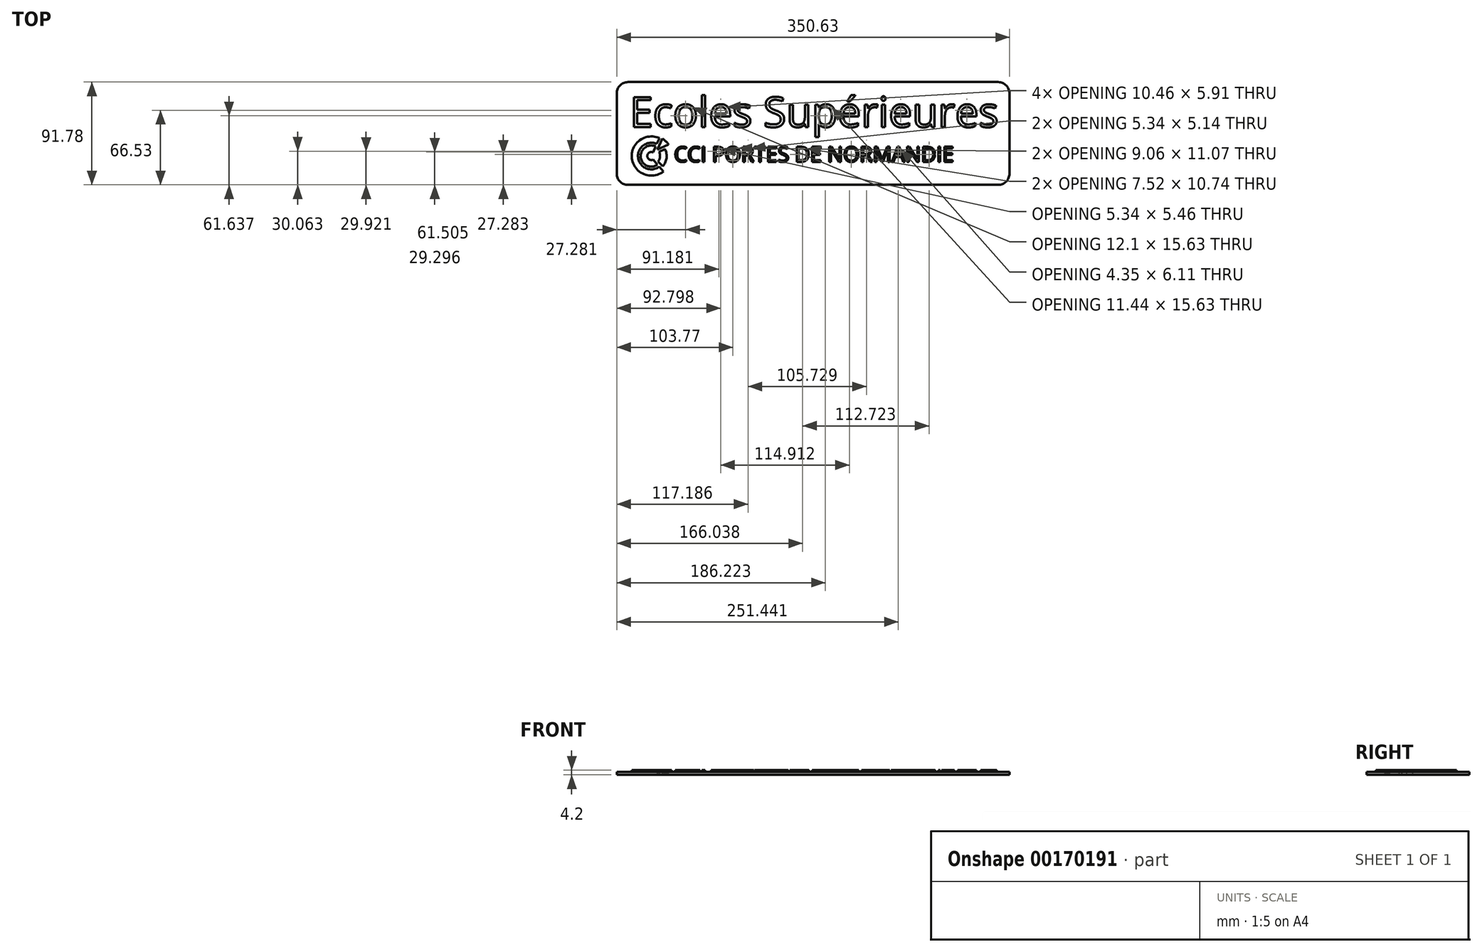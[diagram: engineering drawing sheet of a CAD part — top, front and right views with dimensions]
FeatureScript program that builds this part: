
annotation { "Feature Type Name" : "Feature", "Feature Type Description" : "" }
export const myFeature = defineFeature(function(context is Context, id is Id, definition is map)
    precondition{}
    {
        {
            var Q0;
            Q0=qCreatedBy(makeId("Top.planeOp"),FACE);
            var sketch = newSketch(context, id + "F0", { "sketchPlane" : qUnion([Q0])});
            skLineSegment(sketch, "E0.bottom", {"start": v(-153.76, 79.26) * mm, "end": v(196.24, 79.26) * mm});
            skLineSegment(sketch, "E0.top", {"start": v(-153.76, -13.12) * mm, "end": v(196.24, -13.12) * mm});
            skLineSegment(sketch, "E0.left", {"start": v(-153.76, 79.26) * mm, "end": v(-153.76, -13.12) * mm});
            skLineSegment(sketch, "E0.right", {"start": v(196.24, 79.26) * mm, "end": v(196.24, -13.12) * mm});
            skCircle(sketch, "E1", {"center": v(-123.39, 12.33) * mm, "radius": 17.49 * mm});
            skCircle(sketch, "E2", {"center": v(-123.39, 12.33) * mm, "radius": 11.88 * mm});
            skCircle(sketch, "E3", {"center": v(-123.39, 12.33) * mm, "radius": 9.49 * mm});
            skCircle(sketch, "E4", {"center": v(-123.39, 12.33) * mm, "radius": 3.6 * mm});
            skCircle(sketch, "E5", {"center": v(-123.39, 12.33) * mm, "radius": 7.83 * mm});
            skCircle(sketch, "E6", {"center": v(-123.39, 12.33) * mm, "radius": 13.72 * mm});
            skLineSegment(sketch, "E7", {"start": v(-123.39, 12.33) * mm, "end": v(-116.12, 28.24) * mm});
            skLineSegment(sketch, "E8", {"start": v(-112.54, -1.39) * mm, "end": v(-121.72, 9.15) * mm});
            skCircle(sketch, "E9", {"center": v(-123.39, 12.33) * mm, "radius": 18.48 * mm});
            skLineSegment(sketch, "E10", {"start": v(-118.04, 18.06) * mm, "end": v(-113.59, 28) * mm});
            skLineSegment(sketch, "E11", {"start": v(-118.04, 18.06) * mm, "end": v(-107.93, 22.47) * mm});
            skLineSegment(sketch, "E12", {"start": v(-116.5, 16.06) * mm, "end": v(-111.14, 18.51) * mm});
            skLineSegment(sketch, "E13", {"start": v(-117.25, 7.47) * mm, "end": v(-113.21, 3.13) * mm});
            skText(sketch, "E14", { "text": "Ecoles Supérieures", "fontName": "OpenSans-Regular.ttf"});
            skText(sketch, "E15", { "text": "CCI PORTES DE NORMANDIE", "fontName": "OpenSans-Regular.ttf"});
            const initialGuessF0  = {"E14": [-0.14265, 0.03824, 1, 0, 0.02692], "E15": [-0.10308, 0.00715, 1, 0, 0.01356]};
            skSetInitialGuess(sketch, initialGuessF0);
            skSolve(sketch);
        }
        {
            var Q0;
            Q0=makeQuery(id+"F0.imprint","IMPRINT",FACE,{"disambiguationData":[TD([[makeQuery(id+"F0.imprint","IMPRINT",EDGE,{"derivedFrom":sQuery(id+"F0.wireOp",EDGE,"E14.sketch_text.stroke-0")}),-1.0]])]});
            var Q1;
            Q1=makeQuery(id+"F0.imprint","IMPRINT",FACE,{"disambiguationData":[TD([[makeQuery(id+"F0.imprint","IMPRINT",EDGE,{"derivedFrom":sQuery(id+"F0.wireOp",EDGE,"E14.sketch_text.stroke-12")}),-1.0]])]});
            var Q2;
            Q2=makeQuery(id+"F0.imprint","IMPRINT",FACE,{"disambiguationData":[TD([[makeQuery(id+"F0.imprint","IMPRINT",EDGE,{"derivedFrom":sQuery(id+"F0.wireOp",EDGE,"E14.sketch_text.stroke-27")}),-1.0]])]});
            var Q3;
            Q3=makeQuery(id+"F0.imprint","IMPRINT",FACE,{"disambiguationData":[TD([[makeQuery(id+"F0.imprint","IMPRINT",EDGE,{"derivedFrom":sQuery(id+"F0.wireOp",EDGE,"E14.sketch_text.stroke-44")}),-1.0]])]});
            var Q4;
            Q4=makeQuery(id+"F0.imprint","IMPRINT",FACE,{"disambiguationData":[TD([[makeQuery(id+"F0.imprint","IMPRINT",EDGE,{"derivedFrom":sQuery(id+"F0.wireOp",EDGE,"E14.sketch_text.stroke-48")}),-1.0]])]});
            var Q5;
            Q5=makeQuery(id+"F0.imprint","IMPRINT",FACE,{"disambiguationData":[TD([[makeQuery(id+"F0.imprint","IMPRINT",EDGE,{"derivedFrom":sQuery(id+"F0.wireOp",EDGE,"E14.sketch_text.stroke-67")}),-1.0]])]});
            var Q6;
            Q6=makeQuery(id+"F0.imprint","IMPRINT",FACE,{"disambiguationData":[TD([[makeQuery(id+"F0.imprint","IMPRINT",EDGE,{"derivedFrom":sQuery(id+"F0.wireOp",EDGE,"E14.sketch_text.stroke-92")}),-1.0]])]});
            var Q7;
            Q7=makeQuery(id+"F0.imprint","IMPRINT",FACE,{"disambiguationData":[TD([[makeQuery(id+"F0.imprint","IMPRINT",EDGE,{"derivedFrom":sQuery(id+"F0.wireOp",EDGE,"E14.sketch_text.stroke-117")}),-1.0]])]});
            var Q8;
            Q8=makeQuery(id+"F0.imprint","IMPRINT",FACE,{"disambiguationData":[TD([[makeQuery(id+"F0.imprint","IMPRINT",EDGE,{"derivedFrom":sQuery(id+"F0.wireOp",EDGE,"E14.sketch_text.stroke-134")}),-1.0]])]});
            var Q9;
            Q9=makeQuery(id+"F0.imprint","IMPRINT",FACE,{"disambiguationData":[TD([[makeQuery(id+"F0.imprint","IMPRINT",EDGE,{"derivedFrom":sQuery(id+"F0.wireOp",EDGE,"E15.sketch_text.stroke-34")}),-1.0]])]});
            var Q10;
            Q10=makeQuery(id+"F0.imprint","IMPRINT",FACE,{"disambiguationData":[TD([[makeQuery(id+"F0.imprint","IMPRINT",EDGE,{"derivedFrom":sQuery(id+"F0.wireOp",EDGE,"E15.sketch_text.stroke-49")}),-1.0]])]});
            var Q11;
            Q11=makeQuery(id+"F0.imprint","IMPRINT",FACE,{"disambiguationData":[TD([[makeQuery(id+"F0.imprint","IMPRINT",EDGE,{"derivedFrom":sQuery(id+"F0.wireOp",EDGE,"E15.sketch_text.stroke-65")}),-1.0]])]});
            var Q12;
            Q12=makeQuery(id+"F0.imprint","IMPRINT",FACE,{"disambiguationData":[TD([[makeQuery(id+"F0.imprint","IMPRINT",EDGE,{"derivedFrom":sQuery(id+"F0.wireOp",EDGE,"E15.sketch_text.stroke-83")}),-1.0]])]});
            var Q13;
            Q13=makeQuery(id+"F0.imprint","IMPRINT",FACE,{"disambiguationData":[TD([[makeQuery(id+"F0.imprint","IMPRINT",EDGE,{"derivedFrom":sQuery(id+"F0.wireOp",EDGE,"E15.sketch_text.stroke-91")}),-1.0]])]});
            var Q14;
            Q14=makeQuery(id+"F0.imprint","IMPRINT",FACE,{"disambiguationData":[TD([[makeQuery(id+"F0.imprint","IMPRINT",EDGE,{"derivedFrom":sQuery(id+"F0.wireOp",EDGE,"E15.sketch_text.stroke-0")}),-1.0]])]});
            var Q15;
            Q15=makeQuery(id+"F0.imprint","IMPRINT",FACE,{"disambiguationData":[TD([[makeQuery(id+"F0.imprint","IMPRINT",EDGE,{"derivedFrom":sQuery(id+"F0.wireOp",EDGE,"E15.sketch_text.stroke-15")}),-1.0]])]});
            var Q16;
            Q16=makeQuery(id+"F0.imprint","IMPRINT",FACE,{"disambiguationData":[TD([[makeQuery(id+"F0.imprint","IMPRINT",EDGE,{"derivedFrom":sQuery(id+"F0.wireOp",EDGE,"E15.sketch_text.stroke-30")}),-1.0]])]});
            var Q17;
            Q17=makeQuery(id+"F0.imprint","IMPRINT",FACE,{"disambiguationData":[TD([[makeQuery(id+"F0.imprint","IMPRINT",EDGE,{"derivedFrom":sQuery(id+"F0.wireOp",EDGE,"E14.sketch_text.stroke-159")}),-1.0]])]});
            var Q18;
            Q18=makeQuery(id+"F0.imprint","IMPRINT",FACE,{"disambiguationData":[TD([[makeQuery(id+"F0.imprint","IMPRINT",EDGE,{"derivedFrom":sQuery(id+"F0.wireOp",EDGE,"E14.sketch_text.stroke-178")}),-1.0]])]});
            var Q19;
            Q19=makeQuery(id+"F0.imprint","IMPRINT",FACE,{"disambiguationData":[TD([[makeQuery(id+"F0.imprint","IMPRINT",EDGE,{"derivedFrom":sQuery(id+"F0.wireOp",EDGE,"E14.sketch_text.stroke-186")}),-1.0]])]});
            var Q20;
            Q20=makeQuery(id+"F0.imprint","IMPRINT",FACE,{"disambiguationData":[TD([[makeQuery(id+"F0.imprint","IMPRINT",EDGE,{"derivedFrom":sQuery(id+"F0.wireOp",EDGE,"E14.sketch_text.stroke-230")}),-1.0]])]});
            var Q21;
            Q21=makeQuery(id+"F0.imprint","IMPRINT",FACE,{"disambiguationData":[TD([[makeQuery(id+"F0.imprint","IMPRINT",EDGE,{"derivedFrom":sQuery(id+"F0.wireOp",EDGE,"E14.sketch_text.stroke-247")}),-1.0]])]});
            var Q22;
            Q22=makeQuery(id+"F0.imprint","IMPRINT",FACE,{"disambiguationData":[TD([[makeQuery(id+"F0.imprint","IMPRINT",EDGE,{"derivedFrom":sQuery(id+"F0.wireOp",EDGE,"E14.sketch_text.stroke-279")}),-1.0]])]});
            var Q23;
            Q23=makeQuery(id+"F0.imprint","IMPRINT",FACE,{"disambiguationData":[TD([[makeQuery(id+"F0.imprint","IMPRINT",EDGE,{"derivedFrom":sQuery(id+"F0.wireOp",EDGE,"E14.sketch_text.stroke-260")}),-1.0]])]});
            var Q24;
            Q24=makeQuery(id+"F0.imprint","IMPRINT",FACE,{"disambiguationData":[TD([[makeQuery(id+"F0.imprint","IMPRINT",EDGE,{"derivedFrom":sQuery(id+"F0.wireOp",EDGE,"E14.sketch_text.stroke-211")}),-1.0]])]});
            var Q25;
            Q25=makeQuery(id+"F0.imprint","IMPRINT",FACE,{"disambiguationData":[TD([[makeQuery(id+"F0.imprint","IMPRINT",EDGE,{"derivedFrom":sQuery(id+"F0.wireOp",EDGE,"E14.sketch_text.stroke-199")}),-1.0]])]});
            var Q26;
            Q26=makeQuery(id+"F0.imprint","IMPRINT",FACE,{"disambiguationData":[TD([[makeQuery(id+"F0.imprint","IMPRINT",EDGE,{"derivedFrom":sQuery(id+"F0.wireOp",EDGE,"E14.sketch_text.stroke-203")}),-1.0]])]});
            var Q27;
            Q27=makeQuery(id+"F0.imprint","IMPRINT",FACE,{"disambiguationData":[TD([[makeQuery(id+"F0.imprint","IMPRINT",EDGE,{"derivedFrom":sQuery(id+"F0.wireOp",EDGE,"E15.sketch_text.stroke-263")}),-1.0]])]});
            var Q28;
            Q28=makeQuery(id+"F0.imprint","IMPRINT",FACE,{"disambiguationData":[TD([[makeQuery(id+"F0.imprint","IMPRINT",EDGE,{"derivedFrom":sQuery(id+"F0.wireOp",EDGE,"E15.sketch_text.stroke-267")}),-1.0]])]});
            var Q29;
            Q29=makeQuery(id+"F0.imprint","IMPRINT",FACE,{"disambiguationData":[TD([[makeQuery(id+"F0.imprint","IMPRINT",EDGE,{"derivedFrom":sQuery(id+"F0.wireOp",EDGE,"E15.sketch_text.stroke-249")}),-1.0]])]});
            var Q30;
            Q30=makeQuery(id+"F0.imprint","IMPRINT",FACE,{"disambiguationData":[TD([[makeQuery(id+"F0.imprint","IMPRINT",EDGE,{"derivedFrom":sQuery(id+"F0.wireOp",EDGE,"E15.sketch_text.stroke-103")}),-1.0]])]});
            var Q31;
            Q31=makeQuery(id+"F0.imprint","IMPRINT",FACE,{"disambiguationData":[TD([[makeQuery(id+"F0.imprint","IMPRINT",EDGE,{"derivedFrom":sQuery(id+"F0.wireOp",EDGE,"E15.sketch_text.stroke-128")}),-1.0]])]});
            var Q32;
            Q32=makeQuery(id+"F0.imprint","IMPRINT",FACE,{"disambiguationData":[TD([[makeQuery(id+"F0.imprint","IMPRINT",EDGE,{"derivedFrom":sQuery(id+"F0.wireOp",EDGE,"E15.sketch_text.stroke-154")}),-1.0]])]});
            var Q33;
            Q33=makeQuery(id+"F0.imprint","IMPRINT",FACE,{"disambiguationData":[TD([[makeQuery(id+"F0.imprint","IMPRINT",EDGE,{"derivedFrom":sQuery(id+"F0.wireOp",EDGE,"E15.sketch_text.stroke-142")}),-1.0]])]});
            var Q34;
            Q34=makeQuery(id+"F0.imprint","IMPRINT",FACE,{"disambiguationData":[TD([[makeQuery(id+"F0.imprint","IMPRINT",EDGE,{"derivedFrom":sQuery(id+"F0.wireOp",EDGE,"E15.sketch_text.stroke-169")}),-1.0]])]});
            var Q35;
            Q35=makeQuery(id+"F0.imprint","IMPRINT",FACE,{"disambiguationData":[TD([[makeQuery(id+"F0.imprint","IMPRINT",EDGE,{"derivedFrom":sQuery(id+"F0.wireOp",EDGE,"E15.sketch_text.stroke-185")}),-1.0]])]});
            var Q36;
            Q36=makeQuery(id+"F0.imprint","IMPRINT",FACE,{"disambiguationData":[TD([[makeQuery(id+"F0.imprint","IMPRINT",EDGE,{"derivedFrom":sQuery(id+"F0.wireOp",EDGE,"E15.sketch_text.stroke-203")}),-1.0]])]});
            var Q37;
            Q37=makeQuery(id+"F0.imprint","IMPRINT",FACE,{"disambiguationData":[TD([[makeQuery(id+"F0.imprint","IMPRINT",EDGE,{"derivedFrom":sQuery(id+"F0.wireOp",EDGE,"E15.sketch_text.stroke-234")}),-1.0]])]});
            var Q38;
            Q38=makeQuery(id+"F0.imprint","IMPRINT",FACE,{"disambiguationData":[TD([[makeQuery(id+"F0.imprint","IMPRINT",EDGE,{"derivedFrom":sQuery(id+"F0.wireOp",EDGE,"E15.sketch_text.stroke-221")}),-1.0]])]});
            var Q39;
            {var subQ0=sQuery(id+"F0.wireOp",EDGE,"E8");var subQ1=sQuery(id+"F0.wireOp",EDGE,"E4");var subQ2=makeQuery(id+"F0.imprint","INTERSECT",VERTEX,{"derivedFrom":[subQ1,subQ0]});Q39=makeQuery(id+"F0.imprint","IMPRINT",FACE,{"disambiguationData":[TD([[makeQuery(id+"F0.imprint","IMPRINT",EDGE,{"disambiguationData":[TD([[subQ2,1.0]])],"derivedFrom":subQ1}),-1.0]])]});}
            var Q40;
            {var subQ0=sQuery(id+"F0.wireOp",EDGE,"E7");var subQ1=sQuery(id+"F0.wireOp",EDGE,"E3");var subQ2=makeQuery(id+"F0.imprint","INTERSECT",VERTEX,{"derivedFrom":[subQ1,subQ0]});Q40=makeQuery(id+"F0.imprint","IMPRINT",FACE,{"disambiguationData":[TD([[makeQuery(id+"F0.imprint","IMPRINT",EDGE,{"disambiguationData":[TD([[subQ2,-1.0]])],"derivedFrom":subQ1}),1.0]])]});}
            var Q41;
            {var subQ0=sQuery(id+"F0.wireOp",EDGE,"E7");var subQ1=sQuery(id+"F0.wireOp",EDGE,"E2");var subQ2=makeQuery(id+"F0.imprint","INTERSECT",VERTEX,{"derivedFrom":[subQ1,subQ0]});Q41=makeQuery(id+"F0.imprint","IMPRINT",FACE,{"disambiguationData":[TD([[makeQuery(id+"F0.imprint","IMPRINT",EDGE,{"disambiguationData":[TD([[subQ2,-1.0]])],"derivedFrom":subQ1}),-1.0]])]});}
            var Q42;
            {var subQ0=sQuery(id+"F0.wireOp",EDGE,"E7");var subQ1=sQuery(id+"F0.wireOp",EDGE,"E1");var subQ2=makeQuery(id+"F0.imprint","INTERSECT",VERTEX,{"derivedFrom":[subQ1,subQ0]});Q42=makeQuery(id+"F0.imprint","IMPRINT",FACE,{"disambiguationData":[TD([[makeQuery(id+"F0.imprint","IMPRINT",EDGE,{"disambiguationData":[TD([[subQ2,-1.0]])],"derivedFrom":subQ1}),1.0]])]});}
            extrude(context, id + "F1", {"entities" : qUnion([Q0, Q1, Q2, Q3, Q4, Q5, Q6, Q7, Q8, Q9, Q10, Q11, Q12, Q13, Q14, Q15, Q16, Q17, Q18, Q19, Q20, Q21, Q22, Q23, Q24, Q25, Q26, Q27, Q28, Q29, Q30, Q31, Q32, Q33, Q34, Q35, Q36, Q37, Q38, Q39, Q40, Q41, Q42]), "depth" : 1.5 * mm});
        }
        {
            var Q0;
            Q0=makeQuery(id+"F0.imprint","IMPRINT",FACE,{"disambiguationData":[TD([[makeQuery(id+"F0.imprint","IMPRINT",EDGE,{"derivedFrom":sQuery(id+"F0.wireOp",EDGE,"E0.bottom")}),-1.0]])]});
            var sketch = newSketch(context, id + "F2", { "sketchPlane" : qUnion([Q0])});
            skLineSegment(sketch, "E16.bottom", {"start": v(-154.27, -13.4) * mm, "end": v(196.36, -13.4) * mm});
            skLineSegment(sketch, "E16.top", {"start": v(-154.27, 78.37) * mm, "end": v(196.36, 78.37) * mm});
            skLineSegment(sketch, "E16.left", {"start": v(-154.27, -13.4) * mm, "end": v(-154.27, 78.37) * mm});
            skLineSegment(sketch, "E16.right", {"start": v(196.36, -13.4) * mm, "end": v(196.36, 78.37) * mm});
            skSolve(sketch);
        }
        {
            var Q0;
            Q0 = qSketchRegion(id + "F2", true);
            var Q1;
            {var subQ5=makeQuery(id+"F0.imprint","IMPRINT",EDGE,{"derivedFrom":sQuery(id+"F0.wireOp",EDGE,"E0.top")});Q1=makeQuery(id+"F2.imprint","IMPRINT",FACE,{"disambiguationData":[TD([[makeQuery(id+"F2.imprint","IMPRINT",EDGE,{"derivedFrom":subQ5}),1.0]])]});}
            extrude(context, id + "F3", {"entities" : qUnion([Q0, Q1]), "oppositeDirection" : true, "depth" : 2.7 * mm});
        }
        {
            var Q0;
            Q0=makeQuery(id+"F3.opExtrude","SWEPT_EDGE",EDGE,{"disambiguationData":[OSD([sQuery(id+"F2.wireOp",EDGE,"E16.bottom"),sQuery(id+"F2.wireOp",EDGE,"E16.right")])]});
            var Q1;
            Q1=makeQuery(id+"F3.opExtrude","SWEPT_EDGE",EDGE,{"disambiguationData":[OSD([sQuery(id+"F2.wireOp",EDGE,"E16.top"),sQuery(id+"F2.wireOp",EDGE,"E16.right")])]});
            var Q2;
            Q2=makeQuery(id+"F3.opExtrude","SWEPT_EDGE",EDGE,{"disambiguationData":[OSD([sQuery(id+"F2.wireOp",EDGE,"E16.bottom"),sQuery(id+"F2.wireOp",EDGE,"E16.left")])]});
            var Q3;
            Q3=makeQuery(id+"F3.opExtrude","SWEPT_EDGE",EDGE,{"disambiguationData":[OSD([sQuery(id+"F2.wireOp",EDGE,"E16.top"),sQuery(id+"F2.wireOp",EDGE,"E16.left")])]});
            fillet(context, id + "F4", {"entities" : qUnion([Q0, Q1, Q2, Q3]), "radius" : 10 * mm, "tangentPropagation" : true, "allowEdgeOverflow" : false});
        }
        {
            var Q0;
            {var subQ0=sQuery(id+"F0.wireOp",EDGE,"E12");var subQ1=sQuery(id+"F0.wireOp",EDGE,"E3");var subQ2=makeQuery(id+"F0.imprint","INTERSECT",VERTEX,{"derivedFrom":[subQ1,subQ0]});Q0=makeQuery(id+"F0.imprint","IMPRINT",FACE,{"disambiguationData":[TD([[makeQuery(id+"F0.imprint","IMPRINT",EDGE,{"disambiguationData":[TD([[subQ2,1.0]])],"derivedFrom":subQ1}),1.0]])]});}
            var Q1;
            {var subQ0=sQuery(id+"F0.wireOp",EDGE,"E12");var subQ1=sQuery(id+"F0.wireOp",EDGE,"E2");var subQ2=makeQuery(id+"F0.imprint","INTERSECT",VERTEX,{"derivedFrom":[subQ1,subQ0]});Q1=makeQuery(id+"F0.imprint","IMPRINT",FACE,{"disambiguationData":[TD([[makeQuery(id+"F0.imprint","IMPRINT",EDGE,{"disambiguationData":[TD([[subQ2,1.0]])],"derivedFrom":subQ1}),1.0]])]});}
            var Q2;
            {var subQ0=sQuery(id+"F0.wireOp",EDGE,"E12");var subQ1=sQuery(id+"F0.wireOp",EDGE,"E2");var subQ2=makeQuery(id+"F0.imprint","INTERSECT",VERTEX,{"derivedFrom":[subQ1,subQ0]});Q2=makeQuery(id+"F0.imprint","IMPRINT",FACE,{"disambiguationData":[TD([[makeQuery(id+"F0.imprint","IMPRINT",EDGE,{"disambiguationData":[TD([[subQ2,1.0]])],"derivedFrom":subQ1}),-1.0]])]});}
            var Q3;
            {var subQ0=sQuery(id+"F0.wireOp",EDGE,"E11");var subQ1=sQuery(id+"F0.wireOp",EDGE,"E3");var subQ2=makeQuery(id+"F0.imprint","INTERSECT",VERTEX,{"derivedFrom":[subQ1,subQ0]});Q3=makeQuery(id+"F0.imprint","IMPRINT",FACE,{"disambiguationData":[TD([[makeQuery(id+"F0.imprint","IMPRINT",EDGE,{"disambiguationData":[TD([[subQ2,-1.0]])],"derivedFrom":subQ1}),1.0]])]});}
            var Q4;
            {var subQ0=sQuery(id+"F0.wireOp",EDGE,"E11");var subQ1=sQuery(id+"F0.wireOp",EDGE,"E2");var subQ2=makeQuery(id+"F0.imprint","INTERSECT",VERTEX,{"derivedFrom":[subQ1,subQ0]});Q4=makeQuery(id+"F0.imprint","IMPRINT",FACE,{"disambiguationData":[TD([[makeQuery(id+"F0.imprint","IMPRINT",EDGE,{"disambiguationData":[TD([[subQ2,-1.0]])],"derivedFrom":subQ1}),1.0]])]});}
            var Q5;
            {var subQ0=sQuery(id+"F0.wireOp",EDGE,"E10");var subQ1=sQuery(id+"F0.wireOp",EDGE,"E1");var subQ2=makeQuery(id+"F0.imprint","INTERSECT",VERTEX,{"derivedFrom":[subQ1,subQ0]});Q5=makeQuery(id+"F0.imprint","IMPRINT",FACE,{"disambiguationData":[TD([[makeQuery(id+"F0.imprint","IMPRINT",EDGE,{"disambiguationData":[TD([[subQ2,1.0]])],"derivedFrom":subQ1}),1.0]])]});}
            var Q6;
            {var subQ0=sQuery(id+"F0.wireOp",EDGE,"E10");var subQ1=sQuery(id+"F0.wireOp",EDGE,"E1");var subQ2=makeQuery(id+"F0.imprint","INTERSECT",VERTEX,{"derivedFrom":[subQ1,subQ0]});Q6=makeQuery(id+"F0.imprint","IMPRINT",FACE,{"disambiguationData":[TD([[makeQuery(id+"F0.imprint","IMPRINT",EDGE,{"disambiguationData":[TD([[subQ2,1.0]])],"derivedFrom":subQ1}),-1.0]])]});}
            var Q7;
            {var subQ0=sQuery(id+"F0.wireOp",EDGE,"E11");var subQ1=sQuery(id+"F0.wireOp",EDGE,"E2");var subQ2=makeQuery(id+"F0.imprint","INTERSECT",VERTEX,{"derivedFrom":[subQ1,subQ0]});Q7=makeQuery(id+"F0.imprint","IMPRINT",FACE,{"disambiguationData":[TD([[makeQuery(id+"F0.imprint","IMPRINT",EDGE,{"disambiguationData":[TD([[subQ2,-1.0]])],"derivedFrom":subQ1}),-1.0]])]});}
            extrude(context, id + "F5", {"entities" : qUnion([Q0, Q1, Q2, Q3, Q4, Q5, Q6, Q7]), "oppositeDirection" : true, "depth" : 2 * mm, "hasSecondDirection" : true, "secondDirectionOppositeDirection" : false, "secondDirectionDepth" : 1.5 * mm});
        }
    });
